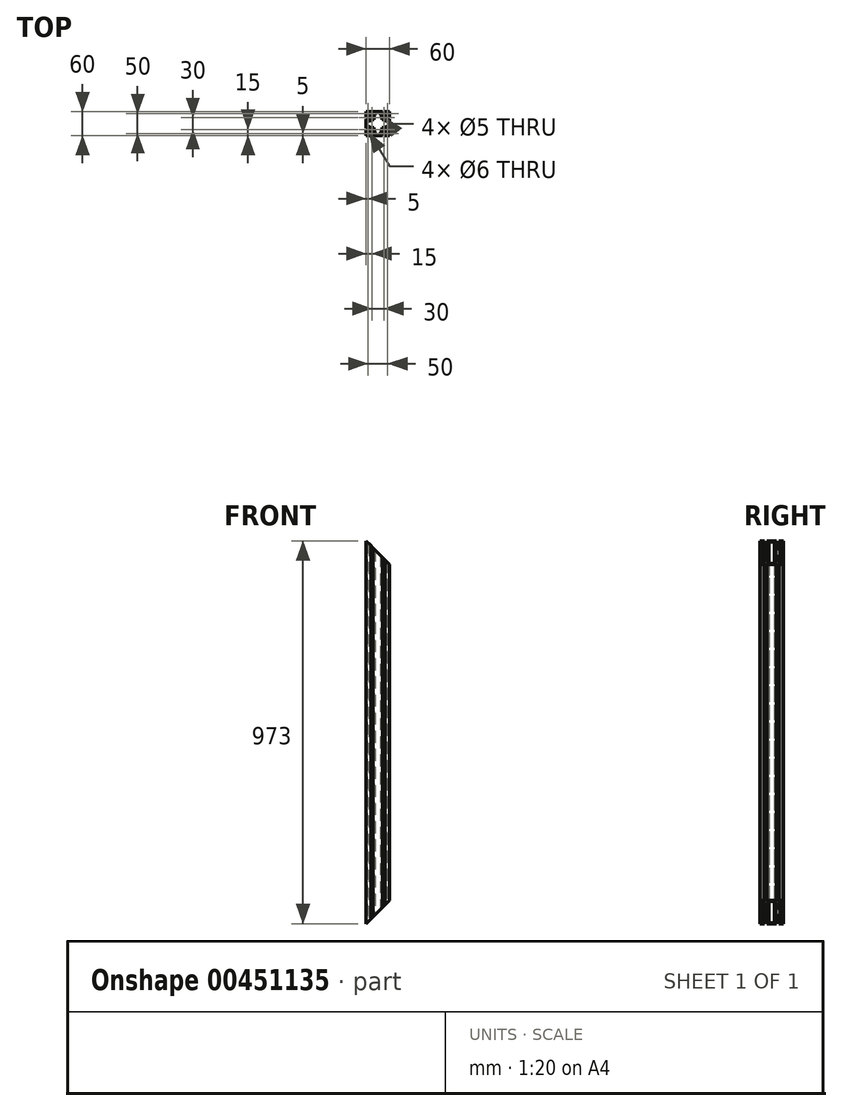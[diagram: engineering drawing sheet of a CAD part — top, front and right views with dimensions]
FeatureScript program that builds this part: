
annotation { "Feature Type Name" : "Feature", "Feature Type Description" : "" }
export const myFeature = defineFeature(function(context is Context, id is Id, definition is map)
    precondition{}
    {
        {
            var Q0;
            Q0=qCreatedBy(makeId("Top.planeOp"),FACE);
            var sketch = newSketch(context, id + "F0", { "sketchPlane" : qUnion([Q0])});
            skLineSegment(sketch, "E0.bottom", {"start": v(30, -30) * mm, "end": v(-30, -30) * mm});
            skLineSegment(sketch, "E0.top", {"start": v(30, 30) * mm, "end": v(-30, 30) * mm});
            skLineSegment(sketch, "E0.left", {"start": v(30, -30) * mm, "end": v(30, 30) * mm});
            skLineSegment(sketch, "E0.right", {"start": v(-30, -30) * mm, "end": v(-30, 30) * mm});
            skPoint(sketch, "E0.middle", {"position": v(0, 0) * mm});
            skLineSegment(sketch, "E1.top", {"start": v(-11.85, 30) * mm, "end": v(-18.15, 30) * mm});
            skLineSegment(sketch, "E1.left", {"start": v(-11.85, 27.5) * mm, "end": v(-11.85, 30) * mm});
            skLineSegment(sketch, "E1.right", {"start": v(-18.15, 27.5) * mm, "end": v(-18.15, 30) * mm});
            skPoint(sketch, "E1.middle", {"position": v(-15, 28.75) * mm});
            skLineSegment(sketch, "E2.bottom", {"start": v(-9.85, 27.5) * mm, "end": v(-11.85, 27.5) * mm});
            skLineSegment(sketch, "E2.left", {"start": v(-9.85, 27.5) * mm, "end": v(-9.85, 21.55) * mm});
            skLineSegment(sketch, "E2.right", {"start": v(-20.15, 27.5) * mm, "end": v(-20.15, 21.55) * mm});
            skPoint(sketch, "E2.middle", {"position": v(-15, 24.52) * mm});
            skArc(sketch, "E3", {"start": v(-20.15, 21.55) * mm, "mid": v(-15, 19.5) * mm, "end": v(-9.85, 21.55) * mm});
            skPoint(sketch, "E4.MirrorP", {"position": v(15, 24.52) * mm});
            skPoint(sketch, "E5.MirrorP", {"position": v(15, 28.75) * mm});
            skLineSegment(sketch, "E6.MirrorCS", {"start": v(11.85, 27.5) * mm, "end": v(11.85, 30) * mm});
            skLineSegment(sketch, "E7.MirrorCS", {"start": v(18.15, 27.5) * mm, "end": v(18.15, 30) * mm});
            skLineSegment(sketch, "E8.MirrorCS", {"start": v(9.85, 27.5) * mm, "end": v(11.85, 27.5) * mm});
            skLineSegment(sketch, "E9.MirrorCS", {"start": v(9.85, 27.5) * mm, "end": v(9.85, 21.55) * mm});
            skArc(sketch, "E10.MirrorCS", {"start": v(20.15, 21.55) * mm, "mid": v(15, 19.5) * mm, "end": v(9.85, 21.55) * mm});
            skLineSegment(sketch, "E11.MirrorCS", {"start": v(20.15, 27.5) * mm, "end": v(20.15, 21.55) * mm});
            skLineSegment(sketch, "E12.MirrorCS", {"start": v(11.85, 30) * mm, "end": v(18.15, 30) * mm});
            skLineSegment(sketch, "E13.1.0", {"start": v(27.5, 20.15) * mm, "end": v(21.55, 20.15) * mm});
            skLineSegment(sketch, "E13.1.1", {"start": v(27.5, 9.85) * mm, "end": v(21.55, 9.85) * mm});
            skArc(sketch, "E13.1.2", {"start": v(21.55, 20.15) * mm, "mid": v(19.5, 15) * mm, "end": v(21.55, 9.85) * mm});
            skLineSegment(sketch, "E13.1.3", {"start": v(27.5, -9.85) * mm, "end": v(21.55, -9.85) * mm});
            skLineSegment(sketch, "E13.1.4", {"start": v(27.5, -20.15) * mm, "end": v(21.55, -20.15) * mm});
            skPoint(sketch, "E13.1.5", {"position": v(28.75, 15) * mm});
            skPoint(sketch, "E13.1.6", {"position": v(28.75, -15) * mm});
            skArc(sketch, "E13.1.7", {"start": v(21.55, -20.15) * mm, "mid": v(19.5, -15) * mm, "end": v(21.55, -9.85) * mm});
            skPoint(sketch, "E13.1.8", {"position": v(24.52, -15) * mm});
            skPoint(sketch, "E13.1.9", {"position": v(24.52, 15) * mm});
            skLineSegment(sketch, "E13.1.10", {"start": v(27.5, 9.85) * mm, "end": v(27.5, 20.15) * mm});
            skLineSegment(sketch, "E13.1.11", {"start": v(27.5, -11.85) * mm, "end": v(27.5, -18.15) * mm});
            skLineSegment(sketch, "E13.1.12", {"start": v(30, 11.85) * mm, "end": v(30, 18.15) * mm});
            skLineSegment(sketch, "E13.1.13", {"start": v(30, -11.85) * mm, "end": v(30, -18.15) * mm});
            skLineSegment(sketch, "E13.1.14", {"start": v(27.5, 18.15) * mm, "end": v(30, 18.15) * mm});
            skLineSegment(sketch, "E13.1.15", {"start": v(27.5, 11.85) * mm, "end": v(30, 11.85) * mm});
            skLineSegment(sketch, "E13.1.16", {"start": v(27.5, 11.85) * mm, "end": v(27.5, 18.15) * mm});
            skLineSegment(sketch, "E13.1.17", {"start": v(27.5, -9.85) * mm, "end": v(27.5, -20.15) * mm});
            skLineSegment(sketch, "E13.1.18", {"start": v(27.5, -18.15) * mm, "end": v(30, -18.15) * mm});
            skLineSegment(sketch, "E13.1.19", {"start": v(27.5, -11.85) * mm, "end": v(30, -11.85) * mm});
            skLineSegment(sketch, "E13.2.0", {"start": v(20.15, -27.5) * mm, "end": v(20.15, -21.55) * mm});
            skLineSegment(sketch, "E13.2.1", {"start": v(9.85, -27.5) * mm, "end": v(9.85, -21.55) * mm});
            skArc(sketch, "E13.2.2", {"start": v(20.15, -21.55) * mm, "mid": v(15, -19.5) * mm, "end": v(9.85, -21.55) * mm});
            skLineSegment(sketch, "E13.2.3", {"start": v(-9.85, -27.5) * mm, "end": v(-9.85, -21.55) * mm});
            skLineSegment(sketch, "E13.2.4", {"start": v(-20.15, -27.5) * mm, "end": v(-20.15, -21.55) * mm});
            skPoint(sketch, "E13.2.5", {"position": v(15, -28.75) * mm});
            skPoint(sketch, "E13.2.6", {"position": v(-15, -28.75) * mm});
            skArc(sketch, "E13.2.7", {"start": v(-20.15, -21.55) * mm, "mid": v(-15, -19.5) * mm, "end": v(-9.85, -21.55) * mm});
            skPoint(sketch, "E13.2.8", {"position": v(-15, -24.52) * mm});
            skPoint(sketch, "E13.2.9", {"position": v(15, -24.52) * mm});
            skLineSegment(sketch, "E13.2.10", {"start": v(9.85, -27.5) * mm, "end": v(20.15, -27.5) * mm});
            skLineSegment(sketch, "E13.2.11", {"start": v(-11.85, -27.5) * mm, "end": v(-18.15, -27.5) * mm});
            skLineSegment(sketch, "E13.2.12", {"start": v(11.85, -30) * mm, "end": v(18.15, -30) * mm});
            skLineSegment(sketch, "E13.2.13", {"start": v(-11.85, -30) * mm, "end": v(-18.15, -30) * mm});
            skLineSegment(sketch, "E13.2.14", {"start": v(18.15, -27.5) * mm, "end": v(18.15, -30) * mm});
            skLineSegment(sketch, "E13.2.15", {"start": v(11.85, -27.5) * mm, "end": v(11.85, -30) * mm});
            skLineSegment(sketch, "E13.2.16", {"start": v(11.85, -27.5) * mm, "end": v(18.15, -27.5) * mm});
            skLineSegment(sketch, "E13.2.17", {"start": v(-9.85, -27.5) * mm, "end": v(-20.15, -27.5) * mm});
            skLineSegment(sketch, "E13.2.18", {"start": v(-18.15, -27.5) * mm, "end": v(-18.15, -30) * mm});
            skLineSegment(sketch, "E13.2.19", {"start": v(-11.85, -27.5) * mm, "end": v(-11.85, -30) * mm});
            skLineSegment(sketch, "E13.3.0", {"start": v(-27.5, -20.15) * mm, "end": v(-21.55, -20.15) * mm});
            skLineSegment(sketch, "E13.3.1", {"start": v(-27.5, -9.85) * mm, "end": v(-21.55, -9.85) * mm});
            skArc(sketch, "E13.3.2", {"start": v(-21.55, -20.15) * mm, "mid": v(-19.5, -15) * mm, "end": v(-21.55, -9.85) * mm});
            skLineSegment(sketch, "E13.3.3", {"start": v(-27.5, 9.85) * mm, "end": v(-21.55, 9.85) * mm});
            skLineSegment(sketch, "E13.3.4", {"start": v(-27.5, 20.15) * mm, "end": v(-21.55, 20.15) * mm});
            skPoint(sketch, "E13.3.5", {"position": v(-28.75, -15) * mm});
            skPoint(sketch, "E13.3.6", {"position": v(-28.75, 15) * mm});
            skArc(sketch, "E13.3.7", {"start": v(-21.55, 20.15) * mm, "mid": v(-19.5, 15) * mm, "end": v(-21.55, 9.85) * mm});
            skPoint(sketch, "E13.3.8", {"position": v(-24.52, 15) * mm});
            skPoint(sketch, "E13.3.9", {"position": v(-24.52, -15) * mm});
            skLineSegment(sketch, "E13.3.10", {"start": v(-27.5, -9.85) * mm, "end": v(-27.5, -20.15) * mm});
            skLineSegment(sketch, "E13.3.11", {"start": v(-27.5, 11.85) * mm, "end": v(-27.5, 18.15) * mm});
            skLineSegment(sketch, "E13.3.12", {"start": v(-30, -11.85) * mm, "end": v(-30, -18.15) * mm});
            skLineSegment(sketch, "E13.3.13", {"start": v(-30, 11.85) * mm, "end": v(-30, 18.15) * mm});
            skLineSegment(sketch, "E13.3.14", {"start": v(-27.5, -18.15) * mm, "end": v(-30, -18.15) * mm});
            skLineSegment(sketch, "E13.3.15", {"start": v(-27.5, -11.85) * mm, "end": v(-30, -11.85) * mm});
            skLineSegment(sketch, "E13.3.16", {"start": v(-27.5, -11.85) * mm, "end": v(-27.5, -18.15) * mm});
            skLineSegment(sketch, "E13.3.17", {"start": v(-27.5, 9.85) * mm, "end": v(-27.5, 20.15) * mm});
            skLineSegment(sketch, "E13.3.18", {"start": v(-27.5, 18.15) * mm, "end": v(-30, 18.15) * mm});
            skLineSegment(sketch, "E13.3.19", {"start": v(-27.5, 11.85) * mm, "end": v(-30, 11.85) * mm});
            skLineSegment(sketch, "E13.anchor1", {"start": v(0, 0) * mm, "end": v(-20.15, 21.55) * mm, "construction": true});
            skLineSegment(sketch, "E13.anchor2", {"start": v(0, 0) * mm, "end": v(-21.55, -20.15) * mm, "construction": true});
            skLineSegment(sketch, "E14.trimOffspring", {"start": v(-18.15, 27.5) * mm, "end": v(-20.15, 27.5) * mm});
            skLineSegment(sketch, "E15.trimOffspring", {"start": v(18.15, 27.5) * mm, "end": v(20.15, 27.5) * mm});
            skCircle(sketch, "E16", {"center": v(-15, 15) * mm, "radius": 2.5 * mm});
            skCircle(sketch, "E17", {"center": v(-25, 25) * mm, "radius": 3 * mm});
            skCircle(sketch, "E18.MirrorC", {"center": v(25, 25) * mm, "radius": 3 * mm});
            skCircle(sketch, "E19.MirrorC", {"center": v(25, -25) * mm, "radius": 3 * mm});
            skCircle(sketch, "E20.MirrorC", {"center": v(-25, -25) * mm, "radius": 3 * mm});
            skCircle(sketch, "E21.MirrorC", {"center": v(15, 15) * mm, "radius": 2.5 * mm});
            skCircle(sketch, "E22.MirrorC", {"center": v(15, -15) * mm, "radius": 2.5 * mm});
            skCircle(sketch, "E23.MirrorC", {"center": v(-15, -15) * mm, "radius": 2.5 * mm});
            skLineSegment(sketch, "E24", {"start": v(-7, 27.5) * mm, "end": v(0, 27.5) * mm});
            skLineSegment(sketch, "E25", {"start": v(-7, 27.5) * mm, "end": v(-7, 22) * mm});
            skLineSegment(sketch, "E26", {"start": v(-10, 10) * mm, "end": v(-10, 16) * mm});
            skLineSegment(sketch, "E27", {"start": v(-10, 16) * mm, "end": v(-7, 22) * mm});
            skLineSegment(sketch, "E28.MirrorCS", {"start": v(10, 10) * mm, "end": v(10, 16) * mm});
            skLineSegment(sketch, "E29.MirrorCS", {"start": v(10, 16) * mm, "end": v(7, 22) * mm});
            skLineSegment(sketch, "E30.MirrorCS", {"start": v(7, 27.5) * mm, "end": v(0, 27.5) * mm});
            skLineSegment(sketch, "E31.MirrorCS", {"start": v(7, 27.5) * mm, "end": v(7, 22) * mm});
            skLineSegment(sketch, "E32.1.0", {"start": v(-10, -10) * mm, "end": v(-16, -10) * mm});
            skLineSegment(sketch, "E32.1.1", {"start": v(-16, -10) * mm, "end": v(-22, -7) * mm});
            skLineSegment(sketch, "E32.1.2", {"start": v(-27.5, -7) * mm, "end": v(-22, -7) * mm});
            skLineSegment(sketch, "E32.1.3", {"start": v(-27.5, -7) * mm, "end": v(-27.5, 0) * mm});
            skLineSegment(sketch, "E32.1.4", {"start": v(-27.5, 7) * mm, "end": v(-27.5, 0) * mm});
            skLineSegment(sketch, "E32.1.5", {"start": v(-27.5, 7) * mm, "end": v(-22, 7) * mm});
            skLineSegment(sketch, "E32.1.6", {"start": v(-16, 10) * mm, "end": v(-22, 7) * mm});
            skLineSegment(sketch, "E32.1.7", {"start": v(-10, 10) * mm, "end": v(-16, 10) * mm});
            skLineSegment(sketch, "E32.2.0", {"start": v(10, -10) * mm, "end": v(10, -16) * mm});
            skLineSegment(sketch, "E32.2.1", {"start": v(10, -16) * mm, "end": v(7, -22) * mm});
            skLineSegment(sketch, "E32.2.2", {"start": v(7, -27.5) * mm, "end": v(7, -22) * mm});
            skLineSegment(sketch, "E32.2.3", {"start": v(7, -27.5) * mm, "end": v(0, -27.5) * mm});
            skLineSegment(sketch, "E32.2.4", {"start": v(-7, -27.5) * mm, "end": v(0, -27.5) * mm});
            skLineSegment(sketch, "E32.2.5", {"start": v(-7, -27.5) * mm, "end": v(-7, -22) * mm});
            skLineSegment(sketch, "E32.2.6", {"start": v(-10, -16) * mm, "end": v(-7, -22) * mm});
            skLineSegment(sketch, "E32.2.7", {"start": v(-10, -10) * mm, "end": v(-10, -16) * mm});
            skLineSegment(sketch, "E32.3.0", {"start": v(10, 10) * mm, "end": v(16, 10) * mm});
            skLineSegment(sketch, "E32.3.1", {"start": v(16, 10) * mm, "end": v(22, 7) * mm});
            skLineSegment(sketch, "E32.3.2", {"start": v(27.5, 7) * mm, "end": v(22, 7) * mm});
            skLineSegment(sketch, "E32.3.3", {"start": v(27.5, 7) * mm, "end": v(27.5, 0) * mm});
            skLineSegment(sketch, "E32.3.4", {"start": v(27.5, -7) * mm, "end": v(27.5, 0) * mm});
            skLineSegment(sketch, "E32.3.5", {"start": v(27.5, -7) * mm, "end": v(22, -7) * mm});
            skLineSegment(sketch, "E32.3.6", {"start": v(16, -10) * mm, "end": v(22, -7) * mm});
            skLineSegment(sketch, "E32.3.7", {"start": v(10, -10) * mm, "end": v(16, -10) * mm});
            skSolve(sketch);
        }
        {
            var Q0;
            {var subQ30=sQuery(id+"F0.wireOp",EDGE,"E1.left");Q0=makeQuery(id+"F0.imprint","IMPRINT",FACE,{"disambiguationData":[TD([[makeQuery(id+"F0.imprint","IMPRINT",EDGE,{"derivedFrom":subQ30}),-1.0]])]});}
            extrude(context, id + "F1", {"entities" : qUnion([Q0]), "depth" : 973 * mm, "offsetDistance" : 25 * mm});
        }
        {
            var Q0;
            Q0=makeQuery(id+"F1.opExtrude","SWEPT_EDGE",EDGE,{"disambiguationData":[OSD([sQuery(id+"F0.wireOp",EDGE,"E24"),sQuery(id+"F0.wireOp",EDGE,"E25")])]});
            var Q1;
            Q1=makeQuery(id+"F1.opExtrude","SWEPT_EDGE",EDGE,{"disambiguationData":[OSD([sQuery(id+"F0.wireOp",EDGE,"E30.MirrorCS"),sQuery(id+"F0.wireOp",EDGE,"E31.MirrorCS")])]});
            var Q2;
            Q2=makeQuery(id+"F1.opExtrude","SWEPT_EDGE",EDGE,{"disambiguationData":[OSD([sQuery(id+"F0.wireOp",EDGE,"840db5bc-c403-45cd-90c7-254e62d9e8c5.3.2"),sQuery(id+"F0.wireOp",EDGE,"840db5bc-c403-45cd-90c7-254e62d9e8c5.3.3")])]});
            var Q3;
            Q3=makeQuery(id+"F1.opExtrude","SWEPT_EDGE",EDGE,{"disambiguationData":[OSD([sQuery(id+"F0.wireOp",EDGE,"840db5bc-c403-45cd-90c7-254e62d9e8c5.3.4"),sQuery(id+"F0.wireOp",EDGE,"840db5bc-c403-45cd-90c7-254e62d9e8c5.3.5")])]});
            var Q4;
            Q4=makeQuery(id+"F1.opExtrude","SWEPT_EDGE",EDGE,{"disambiguationData":[OSD([sQuery(id+"F0.wireOp",EDGE,"840db5bc-c403-45cd-90c7-254e62d9e8c5.1.4"),sQuery(id+"F0.wireOp",EDGE,"840db5bc-c403-45cd-90c7-254e62d9e8c5.1.5")])]});
            var Q5;
            Q5=makeQuery(id+"F1.opExtrude","SWEPT_EDGE",EDGE,{"disambiguationData":[OSD([sQuery(id+"F0.wireOp",EDGE,"840db5bc-c403-45cd-90c7-254e62d9e8c5.1.2"),sQuery(id+"F0.wireOp",EDGE,"840db5bc-c403-45cd-90c7-254e62d9e8c5.1.3")])]});
            var Q6;
            Q6=makeQuery(id+"F1.opExtrude","SWEPT_EDGE",EDGE,{"disambiguationData":[OSD([sQuery(id+"F0.wireOp",EDGE,"840db5bc-c403-45cd-90c7-254e62d9e8c5.2.2"),sQuery(id+"F0.wireOp",EDGE,"840db5bc-c403-45cd-90c7-254e62d9e8c5.2.3")])]});
            var Q7;
            Q7=makeQuery(id+"F1.opExtrude","SWEPT_EDGE",EDGE,{"disambiguationData":[OSD([sQuery(id+"F0.wireOp",EDGE,"840db5bc-c403-45cd-90c7-254e62d9e8c5.2.4"),sQuery(id+"F0.wireOp",EDGE,"840db5bc-c403-45cd-90c7-254e62d9e8c5.2.5")])]});
            fillet(context, id + "F2", {"entities" : qUnion([Q0, Q1, Q2, Q3, Q4, Q5, Q6, Q7]), "radius" : 2 * mm, "tangentPropagation" : true, "allowEdgeOverflow" : false});
        }
        {
            var Q0;
            Q0=makeQuery(id+"F1.opExtrude","SWEPT_EDGE",EDGE,{"disambiguationData":[OSD([sQuery(id+"F0.wireOp",EDGE,"E26"),sQuery(id+"F0.wireOp",EDGE,"E27")])]});
            var Q1;
            Q1=makeQuery(id+"F1.opExtrude","SWEPT_EDGE",EDGE,{"disambiguationData":[OSD([sQuery(id+"F0.wireOp",EDGE,"E28.MirrorCS"),sQuery(id+"F0.wireOp",EDGE,"E29.MirrorCS")])]});
            var Q2;
            Q2=makeQuery(id+"F1.opExtrude","SWEPT_EDGE",EDGE,{"disambiguationData":[OSD([sQuery(id+"F0.wireOp",EDGE,"840db5bc-c403-45cd-90c7-254e62d9e8c5.3.0"),sQuery(id+"F0.wireOp",EDGE,"840db5bc-c403-45cd-90c7-254e62d9e8c5.3.1")])]});
            var Q3;
            Q3=makeQuery(id+"F1.opExtrude","SWEPT_EDGE",EDGE,{"disambiguationData":[OSD([sQuery(id+"F0.wireOp",EDGE,"840db5bc-c403-45cd-90c7-254e62d9e8c5.1.6"),sQuery(id+"F0.wireOp",EDGE,"840db5bc-c403-45cd-90c7-254e62d9e8c5.1.7")])]});
            var Q4;
            Q4=makeQuery(id+"F1.opExtrude","SWEPT_EDGE",EDGE,{"disambiguationData":[OSD([sQuery(id+"F0.wireOp",EDGE,"840db5bc-c403-45cd-90c7-254e62d9e8c5.1.0"),sQuery(id+"F0.wireOp",EDGE,"840db5bc-c403-45cd-90c7-254e62d9e8c5.1.1")])]});
            var Q5;
            Q5=makeQuery(id+"F1.opExtrude","SWEPT_EDGE",EDGE,{"disambiguationData":[OSD([sQuery(id+"F0.wireOp",EDGE,"840db5bc-c403-45cd-90c7-254e62d9e8c5.3.6"),sQuery(id+"F0.wireOp",EDGE,"840db5bc-c403-45cd-90c7-254e62d9e8c5.3.7")])]});
            var Q6;
            Q6=makeQuery(id+"F1.opExtrude","SWEPT_EDGE",EDGE,{"disambiguationData":[OSD([sQuery(id+"F0.wireOp",EDGE,"840db5bc-c403-45cd-90c7-254e62d9e8c5.2.0"),sQuery(id+"F0.wireOp",EDGE,"840db5bc-c403-45cd-90c7-254e62d9e8c5.2.1")])]});
            var Q7;
            Q7=makeQuery(id+"F1.opExtrude","SWEPT_EDGE",EDGE,{"disambiguationData":[OSD([sQuery(id+"F0.wireOp",EDGE,"840db5bc-c403-45cd-90c7-254e62d9e8c5.2.6"),sQuery(id+"F0.wireOp",EDGE,"840db5bc-c403-45cd-90c7-254e62d9e8c5.2.7")])]});
            fillet(context, id + "F3", {"entities" : qUnion([Q0, Q1, Q2, Q3, Q4, Q5, Q6, Q7]), "radius" : 7 * mm, "tangentPropagation" : true, "allowEdgeOverflow" : false});
        }
        {
            var Q0;
            {var subQ0=sQuery(id+"F0.wireOp",EDGE,"E0.bottom");Q0=makeQuery(id+"F1.opExtrude","SWEPT_FACE",FACE,{"disambiguationData":[OSD([subQ0]),TDD([makeQuery(id+"F0.imprint","IMPRINT",EDGE,{"disambiguationData":[TD([[makeQuery(id+"F0.imprint","INTERSECT",VERTEX,{"derivedFrom":[subQ0,sQuery(id+"F0.wireOp",EDGE,"E13.2.12"),sQuery(id+"F0.wireOp",EDGE,"E13.2.15")]}),-1.0]])],"derivedFrom":subQ0})])]});}
            var sketch = newSketch(context, id + "F4", { "sketchPlane" : qUnion([Q0])});
            skLineSegment(sketch, "E33.0", {"start": v(30, 973) * mm, "end": v(30, 0) * mm});
            skLineSegment(sketch, "E33.1", {"start": v(-18.15, 973) * mm, "end": v(-30, 973) * mm});
            skLineSegment(sketch, "E33.2", {"start": v(-18.15, 0) * mm, "end": v(-30, 0) * mm});
            skLineSegment(sketch, "E34", {"start": v(-30, 0) * mm, "end": v(30, 0) * mm});
            skLineSegment(sketch, "E35", {"start": v(30, 60) * mm, "end": v(-30, 0) * mm});
            skLineSegment(sketch, "E36", {"start": v(-30, 973) * mm, "end": v(30, 973) * mm});
            skLineSegment(sketch, "E37", {"start": v(30, 913) * mm, "end": v(-30, 973) * mm});
            skSolve(sketch);
        }
        {
            var Q0;
            Q0=qSketchRegion(id+"F4",true);
            extrude(context, id + "F5", {"entities" : qUnion([Q0]), "operationType" : NewBodyOperationType.REMOVE, "oppositeDirection" : true, "depth" : 60 * mm});
        }
    });
